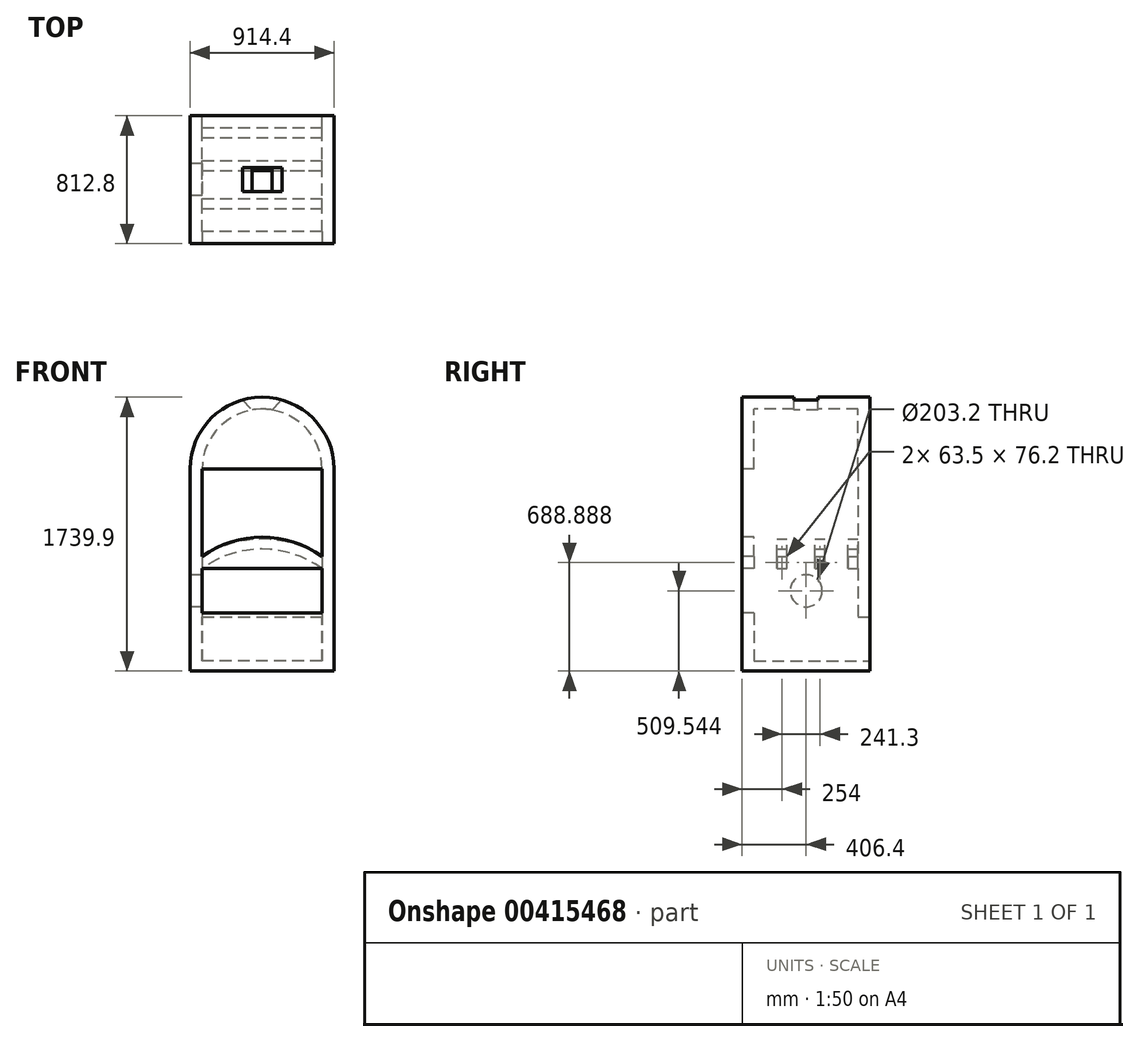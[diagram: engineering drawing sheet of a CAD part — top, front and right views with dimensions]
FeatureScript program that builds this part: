
annotation { "Feature Type Name" : "Feature", "Feature Type Description" : "" }
export const myFeature = defineFeature(function(context is Context, id is Id, definition is map)
    precondition{}
    {
        {
            var Q0;
            Q0=qCreatedBy(makeId("Top.planeOp"),FACE);
            var sketch = newSketch(context, id + "F0", { "sketchPlane" : qUnion([Q0])});
            skLineSegment(sketch, "E0.bottom", {"start": v(457.2, -406.4) * mm, "end": v(-457.2, -406.4) * mm});
            skLineSegment(sketch, "E0.top", {"start": v(457.2, 406.4) * mm, "end": v(-457.2, 406.4) * mm});
            skLineSegment(sketch, "E0.left", {"start": v(457.2, -406.4) * mm, "end": v(457.2, 406.4) * mm});
            skLineSegment(sketch, "E0.right", {"start": v(-457.2, -406.4) * mm, "end": v(-457.2, 406.4) * mm});
            skPoint(sketch, "E0.middle", {"position": v(0, 0) * mm});
            skLineSegment(sketch, "E1.bottom", {"start": v(381, -304.8) * mm, "end": v(-381, -304.8) * mm});
            skLineSegment(sketch, "E1.top", {"start": v(381, 304.8) * mm, "end": v(-381, 304.8) * mm});
            skLineSegment(sketch, "E1.left", {"start": v(381, -304.8) * mm, "end": v(381, 304.8) * mm});
            skLineSegment(sketch, "E1.right", {"start": v(-381, -304.8) * mm, "end": v(-381, 304.8) * mm});
            skSolve(sketch);
        }
        {
            var Q0;
            Q0=makeQuery(id+"F0.imprint","IMPRINT",FACE,{"disambiguationData":[TD([[makeQuery(id+"F0.imprint","IMPRINT",EDGE,{"derivedFrom":sQuery(id+"F0.wireOp",EDGE,"E0.bottom")}),-1.0]])]});
            var Q1;
            Q1=makeQuery(id+"F0.imprint","IMPRINT",FACE,{"disambiguationData":[TD([[makeQuery(id+"F0.imprint","IMPRINT",EDGE,{"derivedFrom":sQuery(id+"F0.wireOp",EDGE,"E1.bottom")}),-1.0]])]});
            extrude(context, id + "F1", {"entities" : qUnion([Q0, Q1]), "depth" : 63.5 * mm});
        }
        {
            var Q0;
            Q0=makeQuery(id+"F1.opExtrude","CAP_FACE",FACE,{"disambiguationData":[OSD([sQuery(id+"F0.wireOp",EDGE,"E0.bottom"),sQuery(id+"F0.wireOp",EDGE,"E0.top"),sQuery(id+"F0.wireOp",EDGE,"E0.left"),sQuery(id+"F0.wireOp",EDGE,"E0.right")])],"isStart":false});
            var sketch = newSketch(context, id + "F2", { "sketchPlane" : qUnion([Q0])});
            skLineSegment(sketch, "E2.bottom", {"start": v(381, -330.2) * mm, "end": v(-381, -330.2) * mm});
            skLineSegment(sketch, "E2.top", {"start": v(381, 330.2) * mm, "end": v(-381, 330.2) * mm});
            skLineSegment(sketch, "E2.left", {"start": v(381, -330.2) * mm, "end": v(381, 330.2) * mm});
            skLineSegment(sketch, "E2.right", {"start": v(-381, -330.2) * mm, "end": v(-381, 330.2) * mm});
            skPoint(sketch, "E2.middle", {"position": v(0, 0) * mm});
            skSolve(sketch);
        }
        {
            var Q0;
            Q0=makeQuery(id+"F2.imprint","IMPRINT",FACE,{"disambiguationData":[TD([[makeQuery(id+"F2.imprint","IMPRINT",EDGE,{"derivedFrom":sQuery(id+"F2.wireOp",EDGE,"E2.bottom")}),1.0]])]});
            extrude(context, id + "F3", {"entities" : qUnion([Q0]), "operationType" : NewBodyOperationType.ADD, "depth" : 1219.2 * mm});
        }
        {
            var Q0;
            {var subQ0=sQuery(id+"F0.wireOp",EDGE,"E0.bottom");Q0=makeQuery(id+"F3.boolean.opBoolean","MERGE",FACE,{"derivedFrom":[makeQuery(id+"F1.opExtrude","SWEPT_FACE",FACE,{"disambiguationData":[OSD([subQ0])]}),makeQuery(id+"F3.opExtrude","SWEPT_FACE",FACE,{"disambiguationData":[OSD([subQ0])]})]});}
            var sketch = newSketch(context, id + "F4", { "sketchPlane" : qUnion([Q0])});
            skCircle(sketch, "E3", {"center": v(0, 1282.7) * mm, "radius": 457.2 * mm});
            skCircle(sketch, "E4", {"center": v(0, 1282.7) * mm, "radius": 381 * mm});
            skPoint(sketch, "E5", {"position": v(0, 1739.9) * mm});
            skPoint(sketch, "E6", {"position": v(0, 1663.7) * mm});
            skArc(sketch, "E7", {"start": v(63.5, 1658.37) * mm, "mid": v(0, 1663.7) * mm, "end": v(-63.5, 1658.37) * mm});
            skLineSegment(sketch, "E8", {"start": v(-125.13, 1722.44) * mm, "end": v(-63.5, 1658.37) * mm});
            skLineSegment(sketch, "E9", {"start": v(63.5, 1658.37) * mm, "end": v(125.13, 1722.44) * mm});
            skSolve(sketch);
        }
        {
            var Q0;
            {var subQ2=sQuery(id+"F0.wireOp",EDGE,"E0.bottom");var subQ3=makeQuery(id+"F3.opExtrude","CAP_EDGE",EDGE,{"disambiguationData":[OSD([subQ2])],"isStart":false});var subQ7=sQuery(id+"F4.wireOp",EDGE,"E4");var subQ8=makeQuery(id+"F4.imprint","INTERSECT",VERTEX,{"disambiguationData":[OD(0.0)],"derivedFrom":[subQ3,subQ7]});Q0=makeQuery(id+"F4.imprint","IMPRINT",FACE,{"disambiguationData":[TD([[makeQuery(id+"F4.imprint","IMPRINT",EDGE,{"disambiguationData":[TD([[subQ8,-1.0]])],"derivedFrom":subQ7}),-1.0]])]});}
            var Q1;
            {var subQ0=sQuery(id+"F4.wireOp",EDGE,"E8");Q1=makeQuery(id+"F4.imprint","IMPRINT",FACE,{"disambiguationData":[TD([[makeQuery(id+"F4.imprint","IMPRINT",EDGE,{"derivedFrom":subQ0}),-1.0]])]});}
            var Q2;
            {var subQ5=sQuery(id+"F4.wireOp",EDGE,"E8");Q2=makeQuery(id+"F4.imprint","IMPRINT",FACE,{"disambiguationData":[TD([[makeQuery(id+"F4.imprint","IMPRINT",EDGE,{"derivedFrom":subQ5}),1.0]])]});}
            var Q3;
            {var subQ0=sQuery(id+"F0.wireOp",EDGE,"E0.top");Q3=makeQuery(id+"F3.boolean.opBoolean","MERGE",FACE,{"derivedFrom":[makeQuery(id+"F1.opExtrude","SWEPT_FACE",FACE,{"disambiguationData":[OSD([subQ0])]}),makeQuery(id+"F3.opExtrude","SWEPT_FACE",FACE,{"disambiguationData":[OSD([subQ0])]})]});}
            extrude(context, id + "F5", {"entities" : qUnion([Q0, Q1, Q2]), "operationType" : NewBodyOperationType.ADD, "endBound" : BoundingType.UP_TO_SURFACE, "oppositeDirection" : true, "endBoundEntityFace" : qUnion([Q3]), "depth" : 25.4 * mm});
        }
        {
            var Q0;
            {var subQ0=sQuery(id+"F2.wireOp",EDGE,"E2.left");var subQ1=sQuery(id+"F2.wireOp",EDGE,"E2.top");var subQ2=sQuery(id+"F2.wireOp",EDGE,"E2.right");var subQ3=sQuery(id+"F0.wireOp",EDGE,"E0.top");Q0=makeQuery(id+"F5.boolean.opBoolean","SPLIT",FACE,{"disambiguationData":[TD([makeQuery(id+"F1.opExtrude","SWEPT_FACE",FACE,{"disambiguationData":[OSD([subQ3])]})])],"derivedFrom":makeQuery(id+"F3.opExtrude","CAP_FACE",FACE,{"disambiguationData":[OSD([sQuery(id+"F0.wireOp",EDGE,"E0.bottom"),subQ3,sQuery(id+"F0.wireOp",EDGE,"E0.left"),sQuery(id+"F0.wireOp",EDGE,"E0.right"),sQuery(id+"F2.wireOp",EDGE,"E2.bottom"),subQ1,subQ0,subQ2])],"isStart":false})});}
            extrude(context, id + "F6", {"entities" : qUnion([Q0]), "operationType" : NewBodyOperationType.ADD, "endBound" : BoundingType.UP_TO_NEXT, "depth" : 25.4 * mm});
        }
        {
            var Q0;
            {var subQ0=sQuery(id+"F0.wireOp",EDGE,"E0.bottom");Q0=makeQuery(id+"F5.boolean.opBoolean","MERGE",FACE,{"derivedFrom":[makeQuery(id+"F3.boolean.opBoolean","MERGE",FACE,{"derivedFrom":[makeQuery(id+"F1.opExtrude","SWEPT_FACE",FACE,{"disambiguationData":[OSD([subQ0])]}),makeQuery(id+"F3.opExtrude","SWEPT_FACE",FACE,{"disambiguationData":[OSD([subQ0])]})]}),makeQuery(id+"F5.opExtrude","CAP_FACE",FACE,{"disambiguationData":[OSD([subQ0,sQuery(id+"F4.wireOp",EDGE,"E3"),sQuery(id+"F4.wireOp",EDGE,"E4")])],"isStart":true})]});}
            var sketch = newSketch(context, id + "F7", { "sketchPlane" : qUnion([Q0])});
            skLineSegment(sketch, "E10.bottom", {"start": v(-381, 1282.7) * mm, "end": v(381, 1282.7) * mm});
            skLineSegment(sketch, "E10.left", {"start": v(-381, 1282.7) * mm, "end": v(-381, 650.79) * mm});
            skLineSegment(sketch, "E10.right", {"start": v(381, 1282.7) * mm, "end": v(381, 650.79) * mm});
            skPoint(sketch, "E11.first.point", {"position": v(0, 774.7) * mm});
            skPoint(sketch, "E11.second.point", {"position": v(381, 650.79) * mm});
            skPoint(sketch, "E11.third.point", {"position": v(-381, 650.79) * mm});
            skPoint(sketch, "E12.first.point", {"position": v(-381, 726.99) * mm});
            skPoint(sketch, "E12.second.point", {"position": v(0, 850.9) * mm});
            skPoint(sketch, "E12.third.point", {"position": v(381, 726.99) * mm});
            skLineSegment(sketch, "E13", {"start": v(-381, 726.99) * mm, "end": v(-381, 650.79) * mm});
            skLineSegment(sketch, "E14", {"start": v(381, 726.99) * mm, "end": v(381, 650.79) * mm});
            skArc(sketch, "E15", {"start": v(381, 726.99) * mm, "mid": v(0, 850.9) * mm, "end": v(-381, 726.99) * mm});
            skArc(sketch, "E16", {"start": v(381, 650.79) * mm, "mid": v(0, 774.7) * mm, "end": v(-381, 650.79) * mm});
            skLineSegment(sketch, "E17", {"start": v(-381, 650.79) * mm, "end": v(-381, 63.5) * mm});
            skLineSegment(sketch, "E18", {"start": v(-381, 63.5) * mm, "end": v(381, 63.5) * mm});
            skLineSegment(sketch, "E19", {"start": v(381, 63.5) * mm, "end": v(381, 650.79) * mm});
            skLineSegment(sketch, "E20", {"start": v(-381, 342.9) * mm, "end": v(381, 342.9) * mm});
            skLineSegment(sketch, "E21", {"start": v(-381, 368.3) * mm, "end": v(381, 368.3) * mm});
            skLineSegment(sketch, "E22", {"start": v(-381, 650.79) * mm, "end": v(381, 650.79) * mm});
            skSolve(sketch);
        }
        {
            var Q0;
            {var subQ0=sQuery(id+"F2.wireOp",EDGE,"E2.left");var subQ1=sQuery(id+"F2.wireOp",EDGE,"E2.right");var subQ2=sQuery(id+"F2.wireOp",EDGE,"E2.bottom");var subQ3=sQuery(id+"F0.wireOp",EDGE,"E0.bottom");Q0=makeQuery(id+"F5.boolean.opBoolean","SPLIT",FACE,{"disambiguationData":[TD([makeQuery(id+"F1.opExtrude","SWEPT_FACE",FACE,{"disambiguationData":[OSD([subQ3])]})])],"derivedFrom":makeQuery(id+"F3.opExtrude","CAP_FACE",FACE,{"disambiguationData":[OSD([subQ3,sQuery(id+"F0.wireOp",EDGE,"E0.top"),sQuery(id+"F0.wireOp",EDGE,"E0.left"),sQuery(id+"F0.wireOp",EDGE,"E0.right"),subQ2,sQuery(id+"F2.wireOp",EDGE,"E2.top"),subQ0,subQ1])],"isStart":false})});}
            extrude(context, id + "F8", {"entities" : qUnion([Q0]), "operationType" : NewBodyOperationType.ADD, "endBound" : BoundingType.UP_TO_NEXT, "depth" : 25.4 * mm});
        }
        {
            var Q0;
            Q0=makeQuery(id+"F7.imprint","IMPRINT",FACE,{"disambiguationData":[TD([[makeQuery(id+"F7.imprint","IMPRINT",EDGE,{"derivedFrom":sQuery(id+"F7.wireOp",EDGE,"E10.bottom")}),1.0]])]});
            var Q1;
            {var subQ0=sQuery(id+"F7.wireOp",EDGE,"E16");Q1=makeQuery(id+"F7.imprint","IMPRINT",FACE,{"disambiguationData":[TD([[makeQuery(id+"F7.imprint","IMPRINT",EDGE,{"derivedFrom":subQ0}),1.0]])]});}
            var Q2;
            {var subQ3=sQuery(id+"F7.wireOp",EDGE,"E21");Q2=makeQuery(id+"F7.imprint","IMPRINT",FACE,{"disambiguationData":[TD([[makeQuery(id+"F7.imprint","IMPRINT",EDGE,{"derivedFrom":subQ3}),1.0]])]});}
            extrude(context, id + "F9", {"entities" : qUnion([Q0, Q1, Q2]), "operationType" : NewBodyOperationType.REMOVE, "endBound" : BoundingType.UP_TO_NEXT, "oppositeDirection" : true, "depth" : 25.4 * mm});
        }
        {
            var Q0;
            Q0=makeQuery(id+"F9.boolean.opBoolean","MERGE",FACE,{"derivedFrom":[makeQuery(id+"F3.opExtrude","SWEPT_FACE",FACE,{"disambiguationData":[OSD([sQuery(id+"F2.wireOp",EDGE,"E2.right")])]}),makeQuery(id+"F9.opExtrude","SWEPT_FACE",FACE,{"disambiguationData":[OSD([sQuery(id+"F7.wireOp",EDGE,"E10.left"),sQuery(id+"F7.wireOp",EDGE,"E13")])]}),makeQuery(id+"F9.opExtrude","SWEPT_FACE",FACE,{"disambiguationData":[OSD([sQuery(id+"F7.wireOp",EDGE,"E17")])]})]});
            var sketch = newSketch(context, id + "F10", { "sketchPlane" : qUnion([Q0])});
            skLineSegment(sketch, "E23", {"start": v(-330.2, 726.99) * mm, "end": v(330.2, 726.99) * mm});
            skLineSegment(sketch, "E24", {"start": v(-330.2, 650.79) * mm, "end": v(330.2, 650.79) * mm});
            skLineSegment(sketch, "E25", {"start": v(266.7, 726.99) * mm, "end": v(266.7, 650.79) * mm});
            skPoint(sketch, "E26", {"position": v(-152.4, 726.99) * mm});
            skPoint(sketch, "E27", {"position": v(88.9, 726.99) * mm});
            skPoint(sketch, "E28", {"position": v(-184.15, 726.99) * mm});
            skPoint(sketch, "E29", {"position": v(-120.65, 726.99) * mm});
            skPoint(sketch, "E30", {"position": v(57.15, 726.99) * mm});
            skPoint(sketch, "E31", {"position": v(120.65, 726.99) * mm});
            skLineSegment(sketch, "E32", {"start": v(-184.15, 726.99) * mm, "end": v(-184.15, 650.79) * mm});
            skLineSegment(sketch, "E33", {"start": v(-184.15, 650.79) * mm, "end": v(-120.65, 650.79) * mm});
            skLineSegment(sketch, "E34", {"start": v(-120.65, 650.79) * mm, "end": v(-120.65, 726.99) * mm});
            skLineSegment(sketch, "E35", {"start": v(57.15, 726.99) * mm, "end": v(57.15, 650.79) * mm});
            skLineSegment(sketch, "E36", {"start": v(57.15, 650.79) * mm, "end": v(120.65, 650.79) * mm});
            skLineSegment(sketch, "E37", {"start": v(120.65, 650.79) * mm, "end": v(120.65, 726.99) * mm});
            skSolve(sketch);
        }
        {
            var Q0;
            {var subQ0=sQuery(id+"F10.wireOp",EDGE,"E32");Q0=makeQuery(id+"F10.imprint","IMPRINT",FACE,{"disambiguationData":[TD([[makeQuery(id+"F10.imprint","IMPRINT",EDGE,{"derivedFrom":subQ0}),1.0]])]});}
            var Q1;
            {var subQ0=sQuery(id+"F10.wireOp",EDGE,"E35");Q1=makeQuery(id+"F10.imprint","IMPRINT",FACE,{"disambiguationData":[TD([[makeQuery(id+"F10.imprint","IMPRINT",EDGE,{"derivedFrom":subQ0}),1.0]])]});}
            var Q2;
            {var subQ3=sQuery(id+"F10.wireOp",EDGE,"E25");Q2=makeQuery(id+"F10.imprint","IMPRINT",FACE,{"disambiguationData":[TD([[makeQuery(id+"F10.imprint","IMPRINT",EDGE,{"derivedFrom":subQ3}),1.0]])]});}
            var Q3;
            Q3=sQuery(id+"F7.wireOp",EDGE,"E16");
            sweep(context, id + "F11", {"operationType" : NewBodyOperationType.ADD, "profiles" : qUnion([Q0, Q1, Q2]), "path" : qUnion([Q3])});
        }
        {
            var Q0;
            {var subQ0=sQuery(id+"F0.wireOp",EDGE,"E0.top");Q0=makeQuery(id+"F6.boolean.opBoolean","MERGE",FACE,{"derivedFrom":[makeQuery(id+"F5.boolean.opBoolean","MERGE",FACE,{"derivedFrom":[makeQuery(id+"F3.boolean.opBoolean","MERGE",FACE,{"derivedFrom":[makeQuery(id+"F1.opExtrude","SWEPT_FACE",FACE,{"disambiguationData":[OSD([subQ0])]}),makeQuery(id+"F3.opExtrude","SWEPT_FACE",FACE,{"disambiguationData":[OSD([subQ0])]})]}),makeQuery(id+"F5.opExtrude","CAP_FACE",FACE,{"disambiguationData":[OSD([subQ0])],"isStart":false})]}),makeQuery(id+"F6.opExtrude","SWEPT_FACE",FACE,{"disambiguationData":[OSD([subQ0])]})]});}
            var sketch = newSketch(context, id + "F12", { "sketchPlane" : qUnion([Q0])});
            skLineSegment(sketch, "E38.bottom", {"start": v(-381, 63.5) * mm, "end": v(381, 63.5) * mm});
            skLineSegment(sketch, "E38.top", {"start": v(-381, 342.9) * mm, "end": v(381, 342.9) * mm});
            skLineSegment(sketch, "E38.left", {"start": v(-381, 63.5) * mm, "end": v(-381, 342.9) * mm});
            skLineSegment(sketch, "E38.right", {"start": v(381, 63.5) * mm, "end": v(381, 342.9) * mm});
            skSolve(sketch);
        }
        {
            var Q0;
            Q0=makeQuery(id+"F12.imprint","IMPRINT",FACE,{"disambiguationData":[TD([[makeQuery(id+"F12.imprint","IMPRINT",EDGE,{"derivedFrom":sQuery(id+"F12.wireOp",EDGE,"E38.bottom")}),1.0]])]});
            extrude(context, id + "F13", {"entities" : qUnion([Q0]), "operationType" : NewBodyOperationType.REMOVE, "oppositeDirection" : true, "depth" : 88.9 * mm});
        }
        {
            var Q0;
            {var subQ0=sQuery(id+"F4.wireOp",EDGE,"E8");Q0=makeQuery(id+"F4.imprint","IMPRINT",FACE,{"disambiguationData":[TD([[makeQuery(id+"F4.imprint","IMPRINT",EDGE,{"derivedFrom":subQ0}),1.0]])]});}
            extrude(context, id + "F14", {"entities" : qUnion([Q0]), "operationType" : NewBodyOperationType.REMOVE, "oppositeDirection" : true, "depth" : 482.6 * mm, "hasSecondDirection" : true, "secondDirectionOppositeDirection" : true, "secondDirectionDepth" : 330.2 * mm});
        }
        {
            var Q0;
            {var subQ0=sQuery(id+"F0.wireOp",EDGE,"E0.right");Q0=makeQuery(id+"F3.boolean.opBoolean","MERGE",FACE,{"derivedFrom":[makeQuery(id+"F1.opExtrude","SWEPT_FACE",FACE,{"disambiguationData":[OSD([subQ0])]}),makeQuery(id+"F3.opExtrude","SWEPT_FACE",FACE,{"disambiguationData":[OSD([subQ0])]})]});}
            var sketch = newSketch(context, id + "F15", { "sketchPlane" : qUnion([Q0])});
            skPoint(sketch, "E39", {"position": v(406.4, 726.99) * mm});
            skPoint(sketch, "E40", {"position": v(406.4, 650.79) * mm});
            skPoint(sketch, "E41", {"position": v(406.4, 368.3) * mm});
            skLineSegment(sketch, "E42", {"start": v(406.4, 650.79) * mm, "end": v(-406.4, 650.79) * mm});
            skLineSegment(sketch, "E43", {"start": v(-406.4, 650.79) * mm, "end": v(-406.4, 368.3) * mm});
            skLineSegment(sketch, "E44", {"start": v(406.4, 650.79) * mm, "end": v(406.4, 368.3) * mm});
            skCircle(sketch, "E45", {"center": v(0, 509.54) * mm, "radius": 101.6 * mm});
            skPoint(sketch, "E45.centerSnap0", {"position": v(406.4, 509.54) * mm});
            skLineSegment(sketch, "E46", {"start": v(406.4, 368.3) * mm, "end": v(-406.4, 368.3) * mm});
            skSolve(sketch);
        }
        {
            var Q0;
            Q0=makeQuery(id+"F15.imprint","IMPRINT",FACE,{"disambiguationData":[TD([[makeQuery(id+"F15.imprint","IMPRINT",EDGE,{"derivedFrom":sQuery(id+"F15.wireOp",EDGE,"E45")}),1.0]])]});
            extrude(context, id + "F16", {"entities" : qUnion([Q0]), "operationType" : NewBodyOperationType.REMOVE, "endBound" : BoundingType.UP_TO_NEXT, "oppositeDirection" : true, "depth" : 25.4 * mm});
        }
        {
            var Q0;
            Q0=makeQuery(id+"F7.imprint","IMPRINT",FACE,{"disambiguationData":[TD([[makeQuery(id+"F7.imprint","IMPRINT",EDGE,{"derivedFrom":sQuery(id+"F7.wireOp",EDGE,"E16")}),1.0]])]});
            var Q1;
            {var subQ0=sQuery(id+"F2.wireOp",EDGE,"E2.bottom");Q1=makeQuery(id+"F9.boolean.opBoolean","SPLIT",FACE,{"disambiguationData":[TD([makeQuery(id+"F9.opExtrude","SWEPT_FACE",FACE,{"disambiguationData":[OSD([sQuery(id+"F7.wireOp",EDGE,"E15")])]})])],"derivedFrom":makeQuery(id+"F8.boolean.opBoolean","MERGE",FACE,{"derivedFrom":[makeQuery(id+"F3.opExtrude","SWEPT_FACE",FACE,{"disambiguationData":[OSD([subQ0])]}),makeQuery(id+"F8.opExtrude","SWEPT_FACE",FACE,{"disambiguationData":[OSD([subQ0])]})]})});}
            extrude(context, id + "F17", {"entities" : qUnion([Q0]), "operationType" : NewBodyOperationType.ADD, "endBound" : BoundingType.UP_TO_SURFACE, "oppositeDirection" : true, "endBoundEntityFace" : qUnion([Q1]), "depth" : 25.4 * mm});
        }
    });
